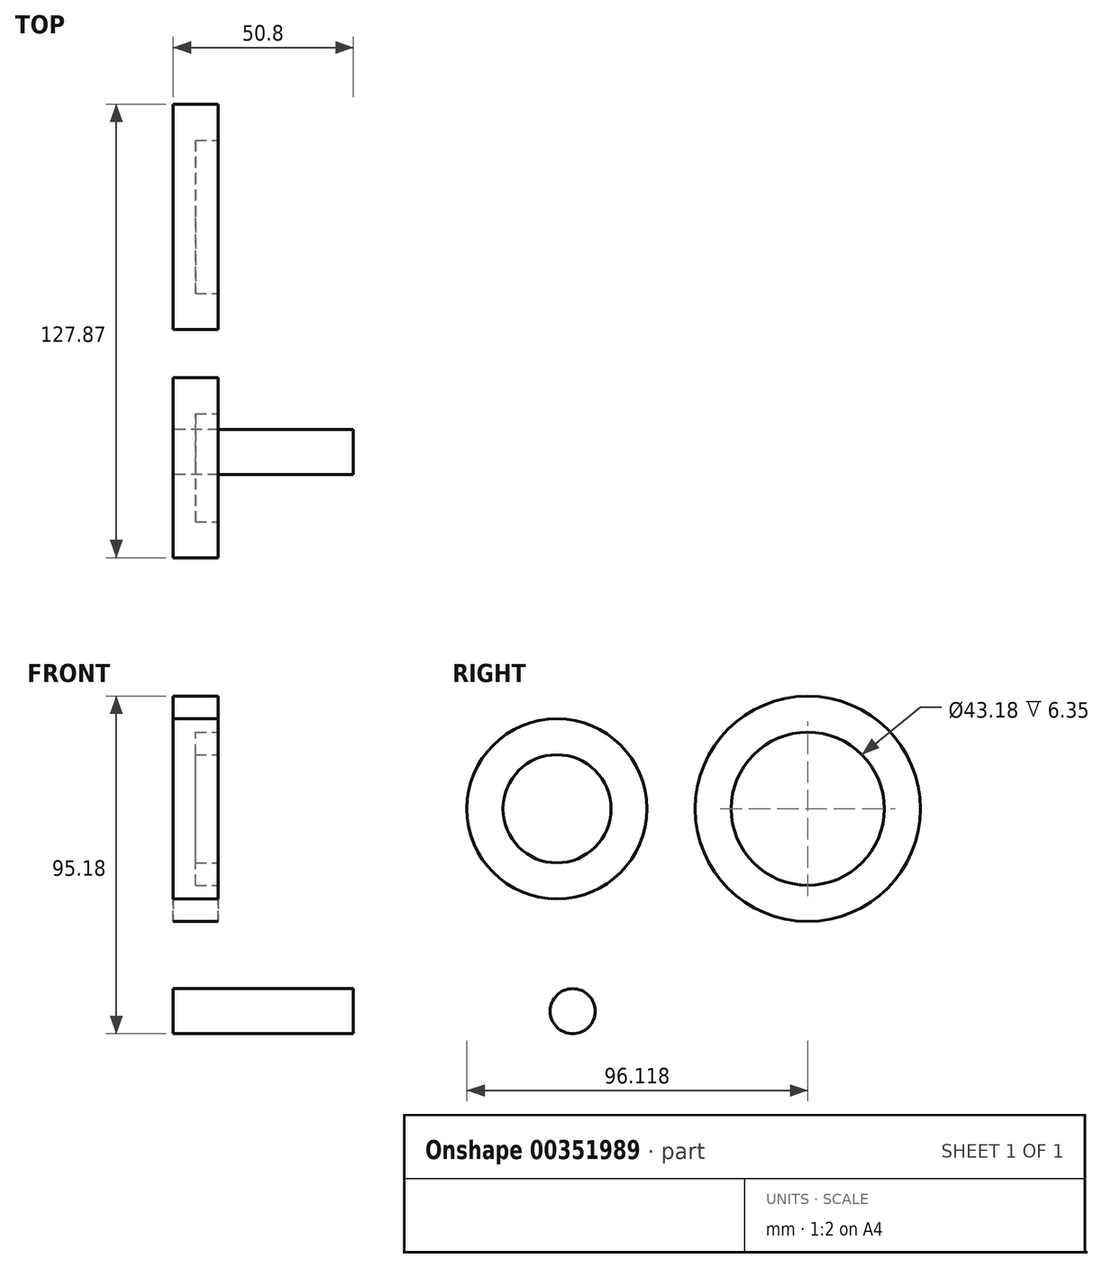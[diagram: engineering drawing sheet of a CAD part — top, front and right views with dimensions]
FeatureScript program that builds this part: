
annotation { "Feature Type Name" : "Feature", "Feature Type Description" : "" }
export const myFeature = defineFeature(function(context is Context, id is Id, definition is map)
    precondition{}
    {
        {
            var Q0;
            Q0=qCreatedBy(makeId("Right.planeOp"),FACE);
            var sketch = newSketch(context, id + "F0", { "sketchPlane" : qUnion([Q0])});
            skCircle(sketch, "E0", {"center": v(-38.77, 31.9) * mm, "radius": 25.4 * mm});
            skCircle(sketch, "E1", {"center": v(31.95, 31.9) * mm, "radius": 31.75 * mm});
            skCircle(sketch, "E2", {"center": v(-34.33, -25.18) * mm, "radius": 6.35 * mm});
            skSolve(sketch);
        }
        {
            var Q0;
            Q0=makeQuery(id+"F0.imprint","IMPRINT",FACE,{"disambiguationData":[TD([[makeQuery(id+"F0.imprint","IMPRINT",EDGE,{"derivedFrom":sQuery(id+"F0.wireOp",EDGE,"E2")}),1.0]])]});
            extrude(context, id + "F1", {"entities" : qUnion([Q0]), "depth" : 50.8 * mm});
        }
        {
            var Q0;
            Q0=makeQuery(id+"F0.imprint","IMPRINT",FACE,{"disambiguationData":[TD([[makeQuery(id+"F0.imprint","IMPRINT",EDGE,{"derivedFrom":sQuery(id+"F0.wireOp",EDGE,"E0")}),1.0]])]});
            var Q1;
            Q1=makeQuery(id+"F0.imprint","IMPRINT",FACE,{"disambiguationData":[TD([[makeQuery(id+"F0.imprint","IMPRINT",EDGE,{"derivedFrom":sQuery(id+"F0.wireOp",EDGE,"E1")}),1.0]])]});
            extrude(context, id + "F2", {"entities" : qUnion([Q0, Q1]), "depth" : 12.7 * mm});
        }
        {
            var Q0;
            Q0=makeQuery(id+"F2.opExtrude","CAP_FACE",FACE,{"disambiguationData":[OSD([sQuery(id+"F0.wireOp",EDGE,"E0")])],"isStart":false});
            var sketch = newSketch(context, id + "F3", { "sketchPlane" : qUnion([Q0])});
            skCircle(sketch, "E3", {"center": v(-38.77, 31.9) * mm, "radius": 15.24 * mm});
            skSolve(sketch);
        }
        {
            var Q0;
            Q0=makeQuery(id+"F2.opExtrude","CAP_FACE",FACE,{"disambiguationData":[OSD([sQuery(id+"F0.wireOp",EDGE,"E1")])],"isStart":false});
            var sketch = newSketch(context, id + "F4", { "sketchPlane" : qUnion([Q0])});
            skCircle(sketch, "E4", {"center": v(31.95, 31.9) * mm, "radius": 21.59 * mm});
            skSolve(sketch);
        }
        {
            var Q0;
            Q0=makeQuery(id+"F3.imprint","IMPRINT",FACE,{"disambiguationData":[TD([[makeQuery(id+"F3.imprint","IMPRINT",EDGE,{"derivedFrom":sQuery(id+"F3.wireOp",EDGE,"E3")}),1.0]])]});
            var Q1;
            Q1=makeQuery(id+"F4.imprint","IMPRINT",FACE,{"disambiguationData":[TD([[makeQuery(id+"F4.imprint","IMPRINT",EDGE,{"derivedFrom":sQuery(id+"F4.wireOp",EDGE,"E4")}),1.0]])]});
            extrude(context, id + "F5", {"entities" : qUnion([Q0, Q1]), "operationType" : NewBodyOperationType.REMOVE, "oppositeDirection" : true, "depth" : 6.35 * mm});
        }
    });
